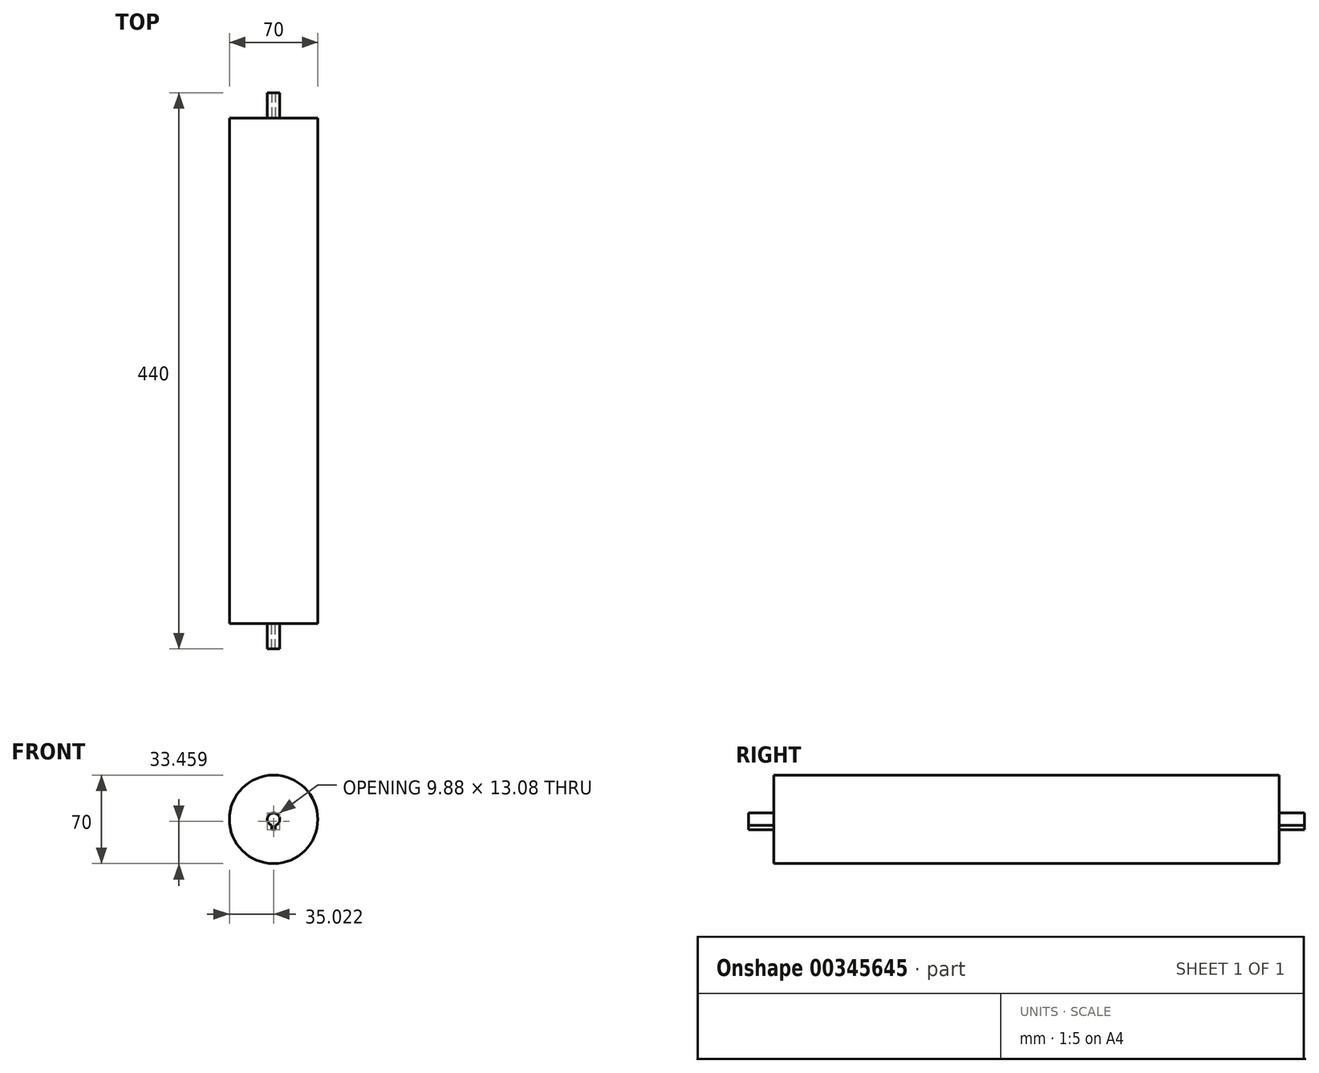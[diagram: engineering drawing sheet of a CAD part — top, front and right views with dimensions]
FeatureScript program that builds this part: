
annotation { "Feature Type Name" : "Feature", "Feature Type Description" : "" }
export const myFeature = defineFeature(function(context is Context, id is Id, definition is map)
    precondition{}
    {
        {
            var Q0;
            Q0=qCreatedBy(makeId("Front.planeOp"),FACE);
            var sketch = newSketch(context, id + "F0", { "sketchPlane" : qUnion([Q0])});
            skCircle(sketch, "E0", {"center": v(0, 0) * mm, "radius": 35 * mm});
            skSolve(sketch);
        }
        {
            var Q0;
            Q0=qSketchRegion(id+"F0",true);
            extrude(context, id + "F1", {"entities" : qUnion([Q0]), "depth" : 400 * mm});
        }
        {
            var Q0;
            Q0=qCreatedBy(makeId("Front.planeOp"),FACE);
            var sketch = newSketch(context, id + "F2", { "sketchPlane" : qUnion([Q0])});
            skCircle(sketch, "E1", {"center": v(0, 0) * mm, "radius": 5 * mm});
            skSolve(sketch);
        }
        {
            var Q0;
            Q0=qSketchRegion(id+"F2",true);
            extrude(context, id + "F3", {"entities" : qUnion([Q0]), "operationType" : NewBodyOperationType.ADD, "oppositeDirection" : true, "depth" : 20 * mm});
        }
        {
            var Q0;
            Q0=qSketchRegion(id+"F2",true);
            extrude(context, id + "F4", {"entities" : qUnion([Q0]), "operationType" : NewBodyOperationType.ADD, "depth" : 420 * mm});
        }
        {
            var Q0;
            Q0=makeQuery(id+"F1.opExtrude","CAP_FACE",FACE,{"disambiguationData":[OSD([sQuery(id+"F0.wireOp",EDGE,"E0")])],"isStart":false});
            var sketch = newSketch(context, id + "F5", { "sketchPlane" : qUnion([Q0])});
            skLineSegment(sketch, "E2", {"start": v(-1.64, -4.72) * mm, "end": v(-1.63, -7.93) * mm});
            skLineSegment(sketch, "E3", {"start": v(-1.63, -7.93) * mm, "end": v(1.37, -8.08) * mm});
            skLineSegment(sketch, "E4", {"start": v(1.37, -8.08) * mm, "end": v(1.36, -4.81) * mm});
            skLineSegment(sketch, "E5", {"start": v(0, 0) * mm, "end": v(-0.13, -8) * mm, "construction": true});
            skSolve(sketch);
        }
        {
            var Q0;
            {var subQ0=sQuery(id+"F5.wireOp",EDGE,"E2");Q0=makeQuery(id+"F5.imprint","IMPRINT",FACE,{"disambiguationData":[TD([[makeQuery(id+"F5.imprint","IMPRINT",EDGE,{"derivedFrom":subQ0}),1.0]])]});}
            extrude(context, id + "F6", {"entities" : qUnion([Q0]), "operationType" : NewBodyOperationType.ADD, "depth" : 40 * mm, "symmetric" : true});
        }
        {
            var Q0;
            {var subQ0=sQuery(id+"F5.wireOp",EDGE,"E2");Q0=makeQuery(id+"F5.imprint","IMPRINT",FACE,{"disambiguationData":[TD([[makeQuery(id+"F5.imprint","IMPRINT",EDGE,{"derivedFrom":subQ0}),1.0]])]});}
            extrude(context, id + "F7", {"entities" : qUnion([Q0]), "operationType" : NewBodyOperationType.ADD, "oppositeDirection" : true, "depth" : 420 * mm});
        }
    });
